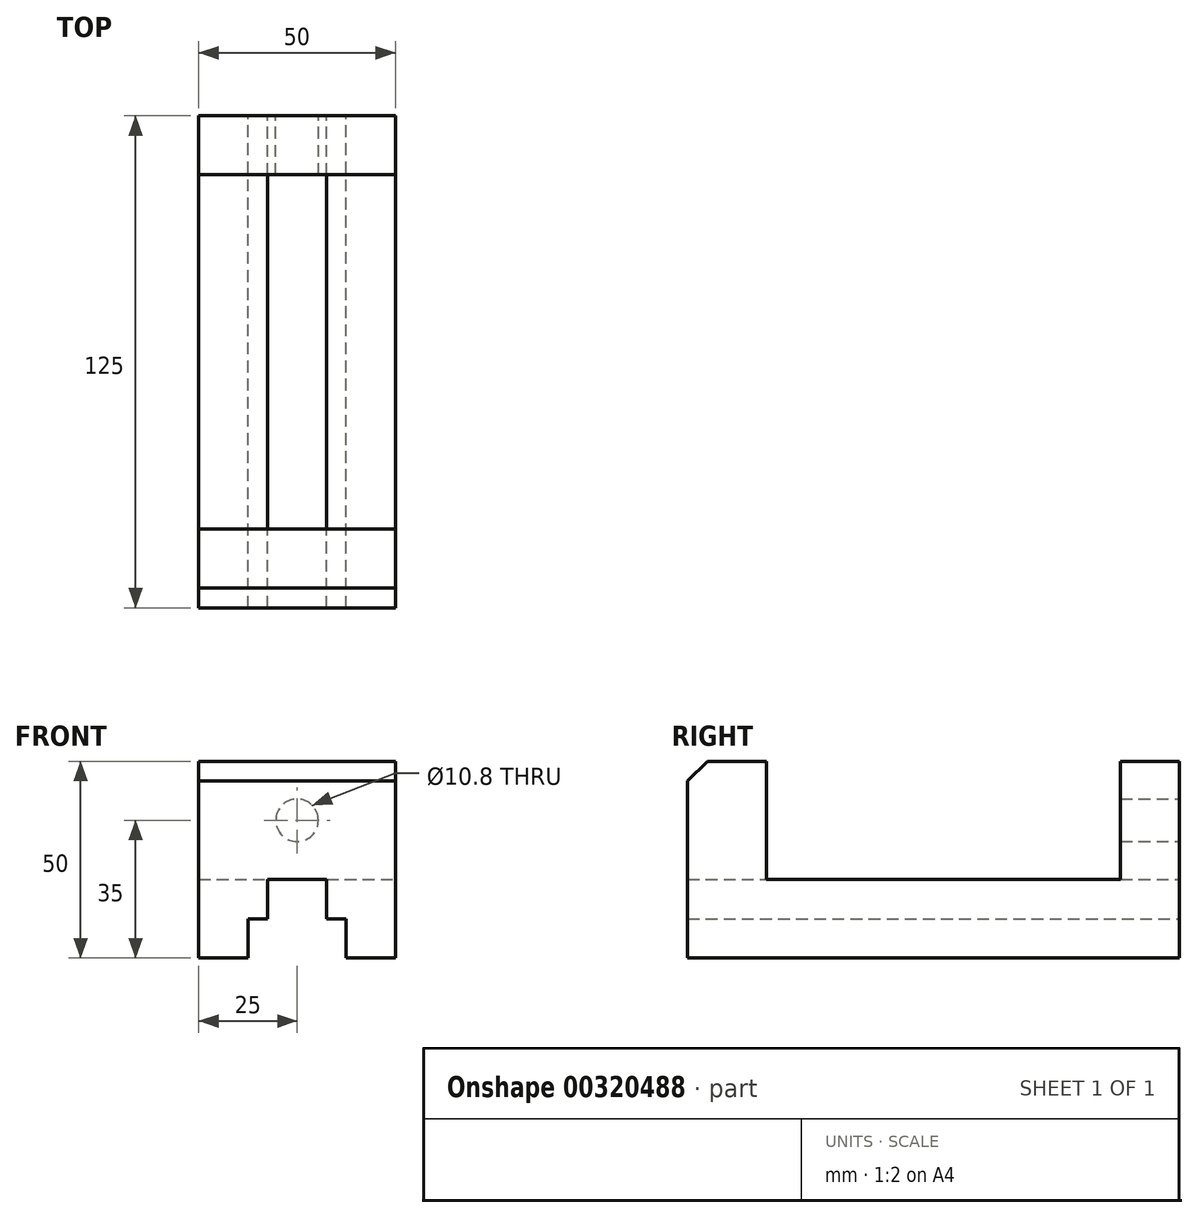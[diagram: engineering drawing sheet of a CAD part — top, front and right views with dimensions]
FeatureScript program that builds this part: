
annotation { "Feature Type Name" : "Feature", "Feature Type Description" : "" }
export const myFeature = defineFeature(function(context is Context, id is Id, definition is map)
    precondition{}
    {
        {
            var Q0;
            Q0=qCreatedBy(makeId("Front.planeOp"),FACE);
            var sketch = newSketch(context, id + "F0", { "sketchPlane" : qUnion([Q0])});
            skLineSegment(sketch, "E0.bottom", {"start": v(-25, 25) * mm, "end": v(25, 25) * mm});
            skLineSegment(sketch, "E0.top", {"start": v(-25, -25) * mm, "end": v(25, -25) * mm});
            skLineSegment(sketch, "E0.left", {"start": v(-25, 25) * mm, "end": v(-25, -25) * mm});
            skLineSegment(sketch, "E0.right", {"start": v(25, 25) * mm, "end": v(25, -25) * mm});
            skPoint(sketch, "E0.middle", {"position": v(0, 0) * mm});
            skSolve(sketch);
        }
        {
            var Q0;
            Q0=makeQuery(id+"F0.imprint","IMPRINT",FACE,{"disambiguationData":[TD([[makeQuery(id+"F0.imprint","IMPRINT",EDGE,{"derivedFrom":sQuery(id+"F0.wireOp",EDGE,"E0.bottom")}),-1.0]])]});
            extrude(context, id + "F1", {"entities" : qUnion([Q0]), "depth" : 125 * mm});
        }
        {
            var Q0;
            Q0=makeQuery(id+"F1.opExtrude","SWEPT_FACE",FACE,{"disambiguationData":[OSD([sQuery(id+"F0.wireOp",EDGE,"E0.right")])]});
            var sketch = newSketch(context, id + "F2", { "sketchPlane" : qUnion([Q0])});
            skLineSegment(sketch, "E1", {"start": v(-15, 25) * mm, "end": v(-15, -25) * mm, "construction": true});
            skLineSegment(sketch, "E2", {"start": v(-125, -5) * mm, "end": v(0, -5) * mm, "construction": true});
            skLineSegment(sketch, "E3", {"start": v(-105, 25) * mm, "end": v(-105, -25) * mm, "construction": true});
            skLineSegment(sketch, "E4.bottom", {"start": v(-105, 25) * mm, "end": v(-15, 25) * mm});
            skLineSegment(sketch, "E4.top", {"start": v(-105, -5) * mm, "end": v(-15, -5) * mm});
            skLineSegment(sketch, "E4.left", {"start": v(-105, 25) * mm, "end": v(-105, -5) * mm});
            skLineSegment(sketch, "E4.right", {"start": v(-15, 25) * mm, "end": v(-15, -5) * mm});
            skSolve(sketch);
        }
        {
            var Q0;
            Q0=makeQuery(id+"F2.imprint","IMPRINT",FACE,{"disambiguationData":[TD([[makeQuery(id+"F2.imprint","IMPRINT",EDGE,{"derivedFrom":sQuery(id+"F2.wireOp",EDGE,"E4.bottom")}),-1.0]])]});
            extrude(context, id + "F3", {"entities" : qUnion([Q0]), "operationType" : NewBodyOperationType.REMOVE, "oppositeDirection" : true, "depth" : 50 * mm});
        }
        {
            var Q0;
            Q0=makeQuery(id+"F1.opExtrude","CAP_FACE",FACE,{"disambiguationData":[OSD([sQuery(id+"F0.wireOp",EDGE,"E0.bottom"),sQuery(id+"F0.wireOp",EDGE,"E0.top"),sQuery(id+"F0.wireOp",EDGE,"E0.left"),sQuery(id+"F0.wireOp",EDGE,"E0.right")])],"isStart":true});
            var sketch = newSketch(context, id + "F4", { "sketchPlane" : qUnion([Q0])});
            skLineSegment(sketch, "E5", {"start": v(0, 28.82) * mm, "end": v(0, -30.5) * mm, "construction": true});
            skLineSegment(sketch, "E6", {"start": v(-32.29, 0) * mm, "end": v(37.06, 0) * mm, "construction": true});
            skLineSegment(sketch, "E7", {"start": v(-25, 10) * mm, "end": v(25, 10) * mm, "construction": true});
            skPoint(sketch, "E8", {"position": v(0, 10) * mm});
            skLineSegment(sketch, "E9.0", {"start": v(-7.5, 28.82) * mm, "end": v(-7.5, -30.5) * mm, "construction": true});
            skLineSegment(sketch, "E10.0", {"start": v(7.5, 28.82) * mm, "end": v(7.5, -30.5) * mm, "construction": true});
            skLineSegment(sketch, "E11.0", {"start": v(-12.5, 28.82) * mm, "end": v(-12.5, -30.5) * mm, "construction": true});
            skLineSegment(sketch, "E12.0", {"start": v(12.5, 28.82) * mm, "end": v(12.5, -30.5) * mm, "construction": true});
            skLineSegment(sketch, "E13", {"start": v(-25, -25) * mm, "end": v(25, -25) * mm, "construction": true});
            skLineSegment(sketch, "E14.0", {"start": v(-25, -15) * mm, "end": v(25, -15) * mm, "construction": true});
            skLineSegment(sketch, "E15.0", {"start": v(-25, -5) * mm, "end": v(25, -5) * mm, "construction": true});
            skLineSegment(sketch, "E16", {"start": v(-12.5, -25) * mm, "end": v(-12.5, -15) * mm});
            skLineSegment(sketch, "E17", {"start": v(-12.5, -15) * mm, "end": v(-7.5, -15) * mm});
            skLineSegment(sketch, "E18", {"start": v(-7.5, -15) * mm, "end": v(-7.5, -5) * mm});
            skLineSegment(sketch, "E19", {"start": v(-7.5, -5) * mm, "end": v(7.5, -5) * mm});
            skLineSegment(sketch, "E20", {"start": v(7.5, -5) * mm, "end": v(7.5, -15) * mm});
            skLineSegment(sketch, "E21", {"start": v(7.5, -15) * mm, "end": v(12.5, -15) * mm});
            skLineSegment(sketch, "E22", {"start": v(12.5, -15) * mm, "end": v(12.5, -25) * mm});
            skSolve(sketch);
        }
        {
            var Q0;
            {var subQ0=sQuery(id+"F4.wireOp",EDGE,"E16");Q0=makeQuery(id+"F4.imprint","IMPRINT",FACE,{"disambiguationData":[TD([[makeQuery(id+"F4.imprint","IMPRINT",EDGE,{"derivedFrom":subQ0}),-1.0]])]});}
            extrude(context, id + "F5", {"entities" : qUnion([Q0]), "operationType" : NewBodyOperationType.REMOVE, "oppositeDirection" : true, "depth" : 125 * mm});
        }
        {
            var Q0;
            Q0=sQuery(id+"F4.wireOp",VERTEX,"E8");
            var Q1;
            Q1=makeQuery(id+"F1.opExtrude","SWEPT_BODY",BODY,{"disambiguationData":[OSD([sQuery(id+"F0.wireOp",EDGE,"E0.bottom"),sQuery(id+"F0.wireOp",EDGE,"E0.top"),sQuery(id+"F0.wireOp",EDGE,"E0.left"),sQuery(id+"F0.wireOp",EDGE,"E0.right")])]});
            hole(context, id + "F6", {"style" : HoleStyle.SIMPLE, "endStyle" : HoleEndStyle.BLIND, "standardTappedOrClearance" : lookupTablePath({ "standard" : "ISO", "engagement" : "75%", "pitch" : "1.25 mm", "size" : "M12", "type" : "Tapped" }), "standardBlindInLast" : lookupTablePath({ "standard" : "ISO", "engagement" : "75%", "pitch" : "1.25 mm", "size" : "M12", "type" : "Tapped" }), "holeDiameter" : 10.8 * mm, "showTappedDepth" : true, "holeDepth" : 15 * mm, "tappedDepth" : 15 * mm, "tapClearance" : 0, "locations" : qUnion([Q0]), "scope" : qUnion([Q1]), "majorDiameter" : 12 * mm});
        }
        {
            var Q0;
            Q0=makeQuery(id+"F1.opExtrude","CAP_EDGE",EDGE,{"disambiguationData":[OSD([sQuery(id+"F0.wireOp",EDGE,"E0.bottom")])],"isStart":false});
            chamfer(context, id + "F7", {"entities" : qUnion([Q0]), "width" : 5 * mm, "tangentPropagation" : true});
        }
    });
